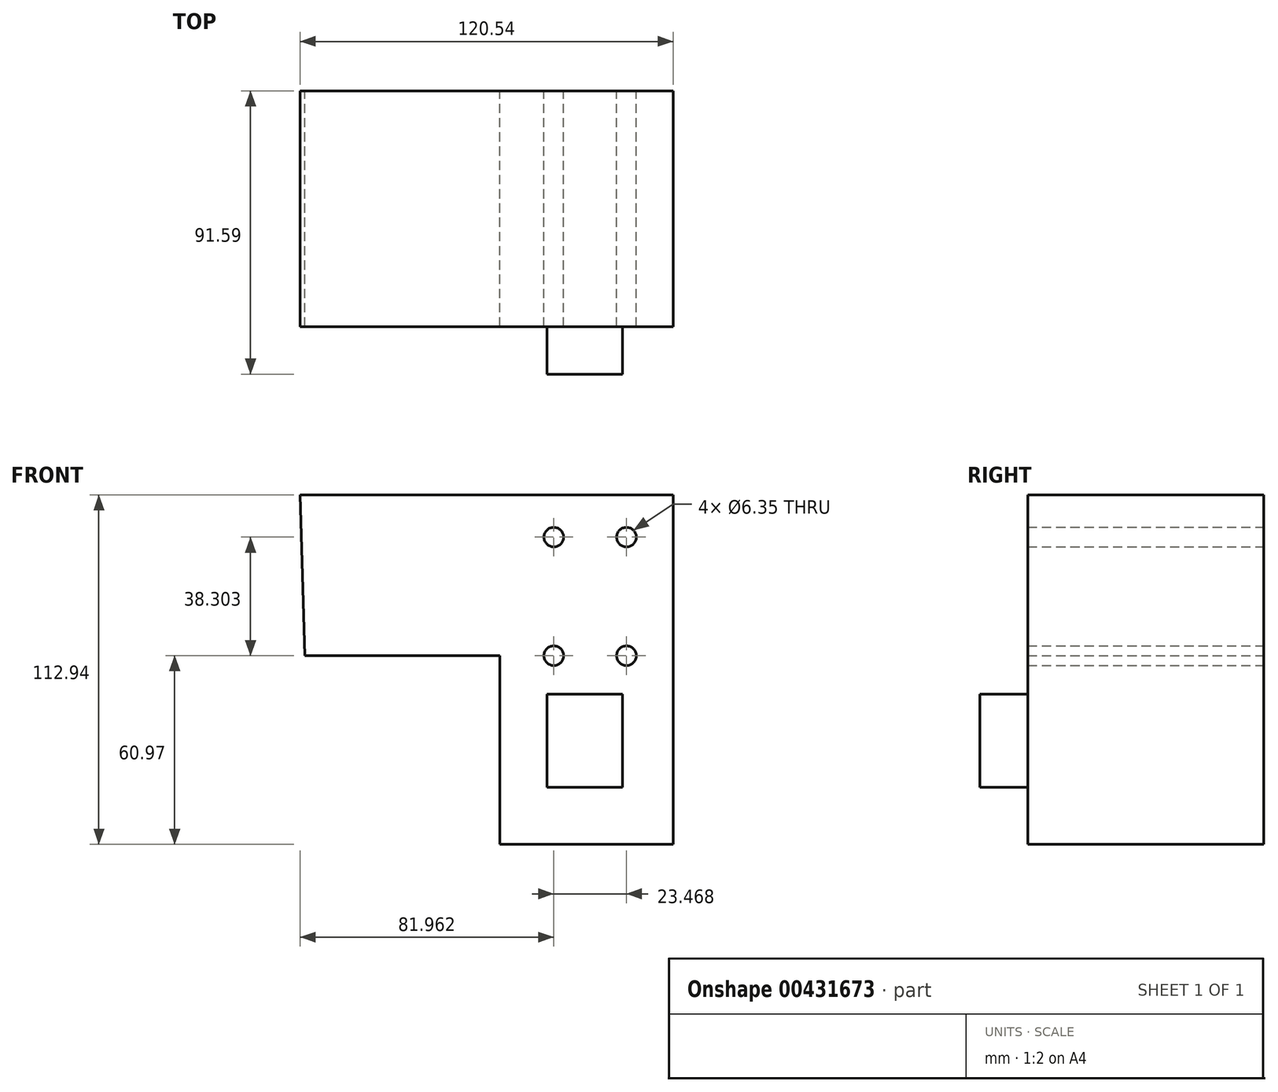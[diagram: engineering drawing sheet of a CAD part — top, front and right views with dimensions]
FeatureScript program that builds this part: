
annotation { "Feature Type Name" : "Feature", "Feature Type Description" : "" }
export const myFeature = defineFeature(function(context is Context, id is Id, definition is map)
    precondition{}
    {
        {
            var Q0;
            Q0=qCreatedBy(makeId("Front.planeOp"),FACE);
            var sketch = newSketch(context, id + "F0", { "sketchPlane" : qUnion([Q0])});
            skLineSegment(sketch, "E0", {"start": v(-63, 0) * mm, "end": v(0, 0) * mm});
            skLineSegment(sketch, "E1", {"start": v(0, 0) * mm, "end": v(0, -60.97) * mm});
            skLineSegment(sketch, "E2", {"start": v(0, -60.97) * mm, "end": v(56, -60.97) * mm});
            skLineSegment(sketch, "E3", {"start": v(56, -60.97) * mm, "end": v(56, 51.97) * mm});
            skLineSegment(sketch, "E4", {"start": v(56, 51.97) * mm, "end": v(-64.54, 51.97) * mm});
            skLineSegment(sketch, "E5", {"start": v(-64.54, 51.97) * mm, "end": v(-63, 0) * mm});
            skSolve(sketch);
        }
        {
            var Q0;
            Q0=makeQuery(id+"F0.imprint","IMPRINT",FACE,{"disambiguationData":[TD([[makeQuery(id+"F0.imprint","IMPRINT",EDGE,{"derivedFrom":sQuery(id+"F0.wireOp",EDGE,"E0")}),1.0]])]});
            extrude(context, id + "F1", {"entities" : qUnion([Q0]), "depth" : 76.2 * mm});
        }
        {
            var Q0;
            Q0=makeQuery(id+"F1.opExtrude","CAP_FACE",FACE,{"disambiguationData":[OSD([sQuery(id+"F0.wireOp",EDGE,"E0"),sQuery(id+"F0.wireOp",EDGE,"E1"),sQuery(id+"F0.wireOp",EDGE,"E2"),sQuery(id+"F0.wireOp",EDGE,"E3"),sQuery(id+"F0.wireOp",EDGE,"E4"),sQuery(id+"F0.wireOp",EDGE,"E5")])],"isStart":true});
            var sketch = newSketch(context, id + "F2", { "sketchPlane" : qUnion([Q0])});
            skLineSegment(sketch, "E6.bottom", {"start": v(-40.9, 0) * mm, "end": v(-17.42, 0) * mm});
            skLineSegment(sketch, "E6.top", {"start": v(-40.9, 38.3) * mm, "end": v(-17.42, 38.3) * mm});
            skLineSegment(sketch, "E6.left", {"start": v(-40.9, 0) * mm, "end": v(-40.9, 38.3) * mm});
            skLineSegment(sketch, "E6.right", {"start": v(-17.42, 0) * mm, "end": v(-17.42, 38.3) * mm});
            skSolve(sketch);
        }
        {
            var Q0;
            Q0=sQuery(id+"F2.wireOp",VERTEX,"E6.left.end");
            var Q1;
            Q1=sQuery(id+"F2.wireOp",VERTEX,"E6.right.end");
            var Q2;
            Q2=sQuery(id+"F2.wireOp",VERTEX,"E6.right.start");
            var Q3;
            Q3=sQuery(id+"F2.wireOp",VERTEX,"E6.left.start");
            var Q4;
            Q4=makeQuery(id+"F1.opExtrude","SWEPT_BODY",BODY,{"disambiguationData":[OSD([sQuery(id+"F0.wireOp",EDGE,"E0"),sQuery(id+"F0.wireOp",EDGE,"E1"),sQuery(id+"F0.wireOp",EDGE,"E2"),sQuery(id+"F0.wireOp",EDGE,"E3"),sQuery(id+"F0.wireOp",EDGE,"E4"),sQuery(id+"F0.wireOp",EDGE,"E5")])]});
            hole(context, id + "F3", {"style" : HoleStyle.SIMPLE, "endStyle" : HoleEndStyle.THROUGH, "holeDiameter" : 6.35 * mm, "isTappedThrough" : true, "tappedDepth" : 12.7 * mm, "tapClearance" : 3, "locations" : qUnion([Q0, Q1, Q2, Q3]), "scope" : qUnion([Q4])});
        }
        {
            var Q0;
            Q0=makeQuery(id+"F1.opExtrude","CAP_FACE",FACE,{"disambiguationData":[OSD([sQuery(id+"F0.wireOp",EDGE,"E0"),sQuery(id+"F0.wireOp",EDGE,"E1"),sQuery(id+"F0.wireOp",EDGE,"E2"),sQuery(id+"F0.wireOp",EDGE,"E3"),sQuery(id+"F0.wireOp",EDGE,"E4"),sQuery(id+"F0.wireOp",EDGE,"E5")])],"isStart":false});
            var sketch = newSketch(context, id + "F4", { "sketchPlane" : qUnion([Q0])});
            skLineSegment(sketch, "E7.bottom", {"start": v(39.63, -42.51) * mm, "end": v(15.26, -42.51) * mm});
            skLineSegment(sketch, "E7.top", {"start": v(39.63, -12.37) * mm, "end": v(15.26, -12.37) * mm});
            skLineSegment(sketch, "E7.left", {"start": v(39.63, -42.51) * mm, "end": v(39.63, -12.37) * mm});
            skLineSegment(sketch, "E7.right", {"start": v(15.26, -42.51) * mm, "end": v(15.26, -12.37) * mm});
            skSolve(sketch);
        }
        {
            var Q0;
            Q0 = qSketchRegion(id + "F4", true);
            extrude(context, id + "F5", {"entities" : qUnion([Q0]), "operationType" : NewBodyOperationType.ADD, "depth" : 15.4 * mm});
        }
    });
